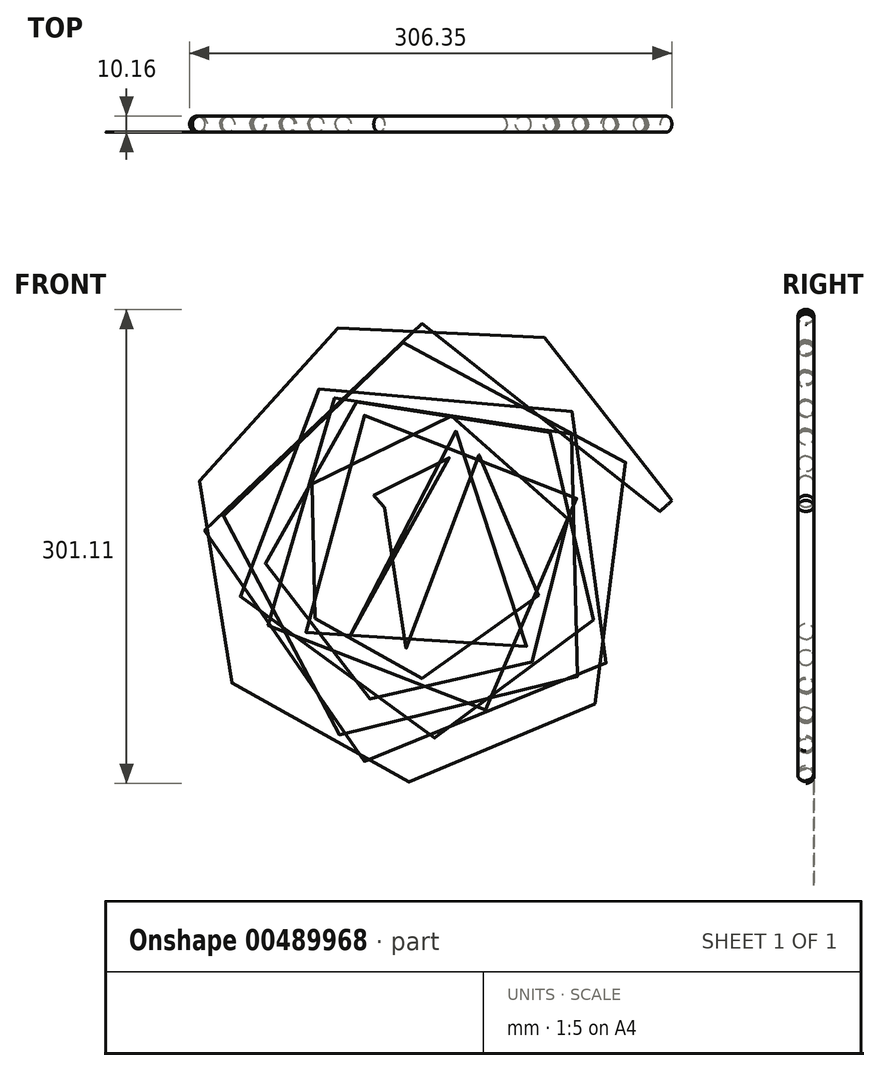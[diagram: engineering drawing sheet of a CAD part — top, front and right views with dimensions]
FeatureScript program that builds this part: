
annotation { "Feature Type Name" : "Feature", "Feature Type Description" : "" }
export const myFeature = defineFeature(function(context is Context, id is Id, definition is map)
    precondition{}
    {
        {
            var Q0;
            Q0=qCreatedBy(makeId("Top.planeOp"),FACE);
            var sketch = newSketch(context, id + "F0", { "sketchPlane" : qUnion([Q0])});
            skCircle(sketch, "E0", {"center": v(0, 0) * mm, "radius": 125 * mm});
            skSolve(sketch);
        }
        {
            var Q0;
            Q0=makeQuery(id+"F0.imprint","IMPRINT",FACE,{"disambiguationData":[TD([[makeQuery(id+"F0.imprint","IMPRINT",EDGE,{"derivedFrom":sQuery(id+"F0.wireOp",EDGE,"E0")}),1.0]])]});
            extrude(context, id + "F1", {"entities" : qUnion([Q0]), "depth" : 25 * mm, "offsetDistance" : 25 * mm});
        }
        {
            var Q0;
            Q0=makeQuery(id+"F1.opExtrude","SWEPT_BODY",BODY,{"disambiguationData":[OSD([sQuery(id+"F0.wireOp",EDGE,"E0")])]});
            deleteBodies(context, id + "F2", {"entities" : qUnion([Q0])});
        }
        {
            var Q0;
            Q0=qCreatedBy(makeId("Front.planeOp"),FACE);
            var sketch = newSketch(context, id + "F3", { "sketchPlane" : qUnion([Q0])});
            skLineSegment(sketch, "E1", {"start": v(0, 0) * mm, "end": v(0, 148.72) * mm});
            skLineSegment(sketch, "E2", {"start": v(0, 148.72) * mm, "end": v(118.91, 0) * mm});
            skLineSegment(sketch, "E3", {"start": v(118.91, 0) * mm, "end": v(0, 0) * mm});
            skSolve(sketch);
        }
        {
            var Q0;
            Q0=makeQuery(id+"F3.imprint","IMPRINT",FACE,{"disambiguationData":[TD([[makeQuery(id+"F3.imprint","IMPRINT",EDGE,{"derivedFrom":sQuery(id+"F3.wireOp",EDGE,"E1")}),-1.0]])]});
            var Q1;
            Q1=sQuery(id+"F3.wireOp",EDGE,"E1");
            revolve(context, id + "F4", {"entities" : qUnion([Q0]), "axis" : qUnion([Q1]), "revolveType" : RevolveType.FULL});
        }
        {
            var Q0;
            Q0=qCreatedBy(makeId("Top.planeOp"),FACE);
            var sketch = newSketch(context, id + "F5", { "sketchPlane" : qUnion([Q0])});
            skFitSpline(sketch, "E4.0", {"points": [v(118.91, 0) * mm, v(118.84, 2.92) * mm, v(118.65, 5.83) * mm, v(118.07, 11.63) * mm, v(117.67, 14.52) * mm, v(116.66, 20.24) * mm, v(116.05, 23.09) * mm, v(114.63, 28.72) * mm, v(113.82, 31.5) * mm, v(111.99, 37) * mm, v(110.97, 39.7) * mm, v(108.75, 45.05) * mm, v(107.54, 47.67) * mm, v(104.93, 52.82) * mm, v(103.54, 55.34) * mm, v(100.56, 60.28) * mm, v(98.99, 62.69) * mm, v(95.67, 67.38) * mm, v(93.92, 69.66) * mm, v(90.27, 74.09) * mm, v(88.37, 76.23) * mm, v(84.4, 80.37) * mm, v(82.36, 82.36) * mm, v(78.11, 86.18) * mm, v(75.92, 88.02) * mm, v(71.42, 91.51) * mm, v(69.1, 93.18) * mm, v(64.36, 96.33) * mm, v(61.94, 97.81) * mm, v(56.99, 100.6) * mm, v(54.46, 101.9) * mm, v(49.33, 104.3) * mm, v(46.73, 105.42) * mm, v(41.44, 107.44) * mm, v(38.77, 108.35) * mm, v(33.36, 109.97) * mm, v(30.63, 110.68) * mm, v(25.13, 111.9) * mm, v(22.36, 112.4) * mm, v(16.8, 113.22) * mm, v(14, 113.52) * mm, v(8.4, 113.92) * mm, v(5.6, 114) * mm, v(0, 114) * mm, v(-2.8, 113.88) * mm, v(-8.37, 113.45) * mm, v(-11.15, 113.13) * mm, v(-16.66, 112.3) * mm, v(-19.4, 111.78) * mm, v(-24.82, 110.54) * mm, v(-27.51, 109.82) * mm, v(-32.82, 108.2) * mm, v(-35.44, 107.28) * mm, v(-40.6, 105.27) * mm, v(-43.15, 104.17) * mm, v(-48.14, 101.79) * mm, v(-50.6, 100.5) * mm, v(-55.39, 97.77) * mm, v(-57.73, 96.31) * mm, v(-62.3, 93.24) * mm, v(-64.52, 91.61) * mm, v(-68.85, 88.22) * mm, v(-70.94, 86.44) * mm, v(-75, 82.74) * mm, v(-76.95, 80.82) * mm, v(-80.7, 76.84) * mm, v(-82.51, 74.78) * mm, v(-85.96, 70.55) * mm, v(-87.6, 68.37) * mm, v(-90.73, 63.9) * mm, v(-92.2, 61.6) * mm, v(-94.99, 56.93) * mm, v(-96.29, 54.54) * mm, v(-98.7, 49.68) * mm, v(-99.83, 47.21) * mm, v(-101.88, 42.2) * mm, v(-102.81, 39.66) * mm, v(-104.49, 34.52) * mm, v(-105.23, 31.92) * mm, v(-106.52, 26.68) * mm, v(-107.07, 24.04) * mm, v(-107.97, 18.73) * mm, v(-108.32, 16.06) * mm, v(-108.82, 10.72) * mm, v(-108.97, 8.04) * mm, v(-109.08, 2.68) * mm, v(-109.04, 0) * mm, v(-108.75, -5.34) * mm, v(-108.5, -8) * mm, v(-107.83, -13.3) * mm, v(-107.4, -15.93) * mm, v(-106.33, -21.15) * mm, v(-105.7, -23.74) * mm, v(-104.27, -28.86) * mm, v(-103.45, -31.38) * mm, v(-101.64, -36.37) * mm, v(-100.65, -38.83) * mm, v(-98.48, -43.65) * mm, v(-97.3, -46.03) * mm, v(-94.8, -50.67) * mm, v(-93.45, -52.94) * mm, v(-90.61, -57.38) * mm, v(-89.11, -59.55) * mm, v(-85.96, -63.75) * mm, v(-84.3, -65.8) * mm, v(-80.86, -69.75) * mm, v(-79.07, -71.67) * mm, v(-75.35, -75.35) * mm, v(-73.42, -77.12) * mm, v(-69.45, -80.51) * mm, v(-67.4, -82.13) * mm, v(-63.2, -85.22) * mm, v(-61.04, -86.68) * mm, v(-56.63, -89.44) * mm, v(-54.38, -90.73) * mm, v(-49.8, -93.16) * mm, v(-47.45, -94.28) * mm, v(-42.7, -96.35) * mm, v(-40.3, -97.3) * mm, v(-35.43, -99.02) * mm, v(-32.96, -99.78) * mm, v(-27.99, -101.13) * mm, v(-25.48, -101.71) * mm, v(-20.42, -102.69) * mm, v(-17.88, -103.08) * mm, v(-12.79, -103.68) * mm, v(-10.23, -103.89) * mm, v(-5.11, -104.1) * mm, v(-2.55, -104.13) * mm, v(2.55, -103.97) * mm, v(5.1, -103.8) * mm, v(10.17, -103.27) * mm, v(12.7, -102.91) * mm, v(17.7, -102.01) * mm, v(20.19, -101.47) * mm, v(25.1, -100.2) * mm, v(27.53, -99.49) * mm, v(32.33, -97.87) * mm, v(34.7, -96.97) * mm, v(39.36, -95.01) * mm, v(41.65, -93.95) * mm, v(46.14, -91.65) * mm, v(48.33, -90.42) * mm, v(52.63, -87.81) * mm, v(54.73, -86.43) * mm, v(58.82, -83.51) * mm, v(60.8, -81.98) * mm, v(64.65, -78.78) * mm, v(66.52, -77.1) * mm, v(70.11, -73.64) * mm, v(71.84, -71.84) * mm, v(75.17, -68.13) * mm, v(76.76, -66.2) * mm, v(79.8, -62.27) * mm, v(81.24, -60.25) * mm, v(83.96, -56.1) * mm, v(85.25, -53.98) * mm, v(87.66, -49.66) * mm, v(88.79, -47.45) * mm, v(90.87, -42.98) * mm, v(91.82, -40.7) * mm, v(93.57, -36.1) * mm, v(94.35, -33.76) * mm, v(95.75, -29.04) * mm, v(96.35, -26.66) * mm, v(97.4, -21.87) * mm, v(97.83, -19.46) * mm, v(98.51, -14.61) * mm, v(98.76, -12.18) * mm, v(99.09, -7.3) * mm, v(99.16, -4.87) * mm, v(99.12, 0) * mm, v(99.02, 2.43) * mm, v(98.62, 7.28) * mm, v(98.34, 9.69) * mm, v(97.6, 14.48) * mm, v(97.13, 16.86) * mm, v(96.03, 21.57) * mm, v(95.4, 23.9) * mm, v(93.97, 28.5) * mm, v(93.16, 30.78) * mm, v(91.4, 35.26) * mm, v(90.43, 37.46) * mm, v(88.35, 41.79) * mm, v(87.22, 43.9) * mm, v(84.83, 48.06) * mm, v(83.56, 50.09) * mm, v(80.87, 54.04) * mm, v(79.46, 55.96) * mm, v(76.5, 59.7) * mm, v(74.95, 61.5) * mm, v(71.72, 65) * mm, v(70.05, 66.7) * mm, v(66.59, 69.94) * mm, v(64.8, 71.5) * mm, v(61.11, 74.47) * mm, v(59.22, 75.89) * mm, v(55.34, 78.57) * mm, v(53.35, 79.84) * mm, v(49.29, 82.23) * mm, v(47.21, 83.35) * mm, v(43, 85.43) * mm, v(40.86, 86.39) * mm, v(36.5, 88.14) * mm, v(34.3, 88.94) * mm, v(29.85, 90.37) * mm, v(27.6, 91) * mm, v(23.07, 92.1) * mm, v(20.78, 92.56) * mm, v(16.2, 93.32) * mm, v(13.88, 93.6) * mm, v(9.26, 94.02) * mm, v(6.94, 94.14) * mm, v(2.31, 94.22) * mm, v(0, 94.17) * mm, v(-4.61, 93.9) * mm, v(-6.91, 93.68) * mm, v(-11.48, 93.07) * mm, v(-13.75, 92.69) * mm, v(-18.25, 91.75) * mm, v(-20.48, 91.2) * mm, v(-24.89, 89.94) * mm, v(-27.07, 89.22) * mm, v(-31.36, 87.64) * mm, v(-33.47, 86.77) * mm, v(-37.63, 84.88) * mm, v(-39.67, 83.87) * mm, v(-43.66, 81.68) * mm, v(-45.62, 80.52) * mm, v(-49.43, 78.05) * mm, v(-51.29, 76.75) * mm, v(-54.9, 74.02) * mm, v(-56.65, 72.59) * mm, v(-60.04, 69.6) * mm, v(-61.68, 68.05) * mm, v(-64.84, 64.83) * mm, v(-66.35, 63.17) * mm, v(-69.25, 59.74) * mm, v(-70.64, 57.97) * mm, v(-73.27, 54.34) * mm, v(-74.52, 52.48) * mm, v(-76.88, 48.68) * mm, v(-77.98, 46.74) * mm, v(-80.04, 42.78) * mm, v(-81, 40.77) * mm, v(-82.76, 36.68) * mm, v(-83.57, 34.61) * mm, v(-85.02, 30.42) * mm, v(-85.67, 28.3) * mm, v(-86.8, 24.02) * mm, v(-87.29, 21.86) * mm, v(-88.1, 17.52) * mm, v(-88.43, 15.34) * mm, v(-88.92, 10.97) * mm, v(-89.1, 8.77) * mm, v(-89.26, 4.38) * mm, v(-89.26, 2.19) * mm, v(-89.1, -2.19) * mm, v(-88.95, -4.37) * mm, v(-88.47, -8.72) * mm, v(-88.16, -10.88) * mm, v(-87.36, -15.16) * mm, v(-86.89, -17.29) * mm, v(-85.79, -21.49) * mm, v(-85.16, -23.57) * mm, v(-83.75, -27.67) * mm, v(-82.97, -29.7) * mm, v(-81.28, -33.67) * mm, v(-80.35, -35.62) * mm, v(-78.37, -39.45) * mm, v(-77.31, -41.33) * mm, v(-75.06, -44.99) * mm, v(-73.86, -46.78) * mm, v(-71.35, -50.26) * mm, v(-70.04, -51.95) * mm, v(-67.28, -55.22) * mm, v(-65.85, -56.8) * mm, v(-62.87, -59.86) * mm, v(-61.33, -61.33) * mm, v(-58.14, -64.15) * mm, v(-56.5, -65.5) * mm, v(-53.12, -68.07) * mm, v(-51.39, -69.3) * mm, v(-47.84, -71.6) * mm, v(-46.03, -72.69) * mm, v(-42.33, -74.73) * mm, v(-40.45, -75.67) * mm, v(-36.62, -77.43) * mm, v(-34.68, -78.23) * mm, v(-30.74, -79.7) * mm, v(-28.75, -80.35) * mm, v(-24.73, -81.52) * mm, v(-22.7, -82.02) * mm, v(-18.61, -82.89) * mm, v(-16.56, -83.24) * mm, v(-12.43, -83.8) * mm, v(-10.36, -84) * mm, v(-6.21, -84.26) * mm, v(-4.14, -84.3) * mm, v(0, -84.26) * mm, v(2.07, -84.15) * mm, v(6.18, -83.8) * mm, v(8.23, -83.54) * mm, v(12.3, -82.88) * mm, v(14.31, -82.48) * mm, v(18.3, -81.53) * mm, v(20.29, -80.98) * mm, v(24.19, -79.74) * mm, v(26.12, -79.05) * mm, v(29.9, -77.53) * mm, v(31.77, -76.7) * mm, v(35.43, -74.9) * mm, v(37.22, -73.94) * mm, v(40.73, -71.9) * mm, v(42.44, -70.8) * mm, v(45.78, -68.5) * mm, v(47.4, -67.3) * mm, v(50.55, -64.77) * mm, v(52.08, -63.45) * mm, v(55.02, -60.7) * mm, v(56.44, -59.28) * mm, v(59.17, -56.33) * mm, v(60.48, -54.81) * mm, v(62.98, -51.68) * mm, v(64.16, -50.07) * mm, v(66.42, -46.77) * mm, v(67.48, -45.09) * mm, v(69.48, -41.64) * mm, v(70.41, -39.89) * mm, v(72.15, -36.31) * mm, v(72.95, -34.5) * mm, v(74.4, -30.82) * mm, v(75.07, -28.96) * mm, v(76.25, -25.19) * mm, v(76.77, -23.29) * mm, v(77.67, -19.45) * mm, v(78.05, -17.52) * mm, v(78.67, -13.65) * mm, v(78.9, -11.7) * mm, v(79.23, -7.8) * mm, v(79.32, -5.85) * mm, v(79.35, -1.95) * mm, v(79.3, 0) * mm, v(79.05, 3.88) * mm, v(78.85, 5.82) * mm, v(78.32, 9.66) * mm, v(77.98, 11.57) * mm, v(77.17, 15.35) * mm, v(76.7, 17.22) * mm, v(75.6, 20.92) * mm, v(75, 22.75) * mm, v(73.64, 26.35) * mm, v(72.9, 28.12) * mm, v(71.3, 31.6) * mm, v(70.42, 33.31) * mm, v(68.57, 36.65) * mm, v(67.58, 38.29) * mm, v(65.5, 41.47) * mm, v(64.39, 43.03) * mm, v(62.08, 46.04) * mm, v(60.87, 47.5) * mm, v(58.34, 50.33) * mm, v(57.03, 51.7) * mm, v(54.32, 54.32) * mm, v(52.92, 55.58) * mm, v(50.02, 58) * mm, v(48.54, 59.15) * mm, v(45.48, 61.33) * mm, v(43.92, 62.37) * mm, v(40.72, 64.31) * mm, v(39.1, 65.23) * mm, v(35.77, 66.93) * mm, v(34.08, 67.72) * mm, v(30.66, 69.17) * mm, v(28.92, 69.83) * mm, v(25.4, 71.02) * mm, v(23.63, 71.55) * mm, v(20.05, 72.47) * mm, v(18.25, 72.87) * mm, v(14.62, 73.52) * mm, v(12.8, 73.78) * mm, v(9.15, 74.17) * mm, v(7.31, 74.3) * mm, v(3.65, 74.4) * mm, v(1.82, 74.4) * mm, v(-1.82, 74.24) * mm, v(-3.64, 74.1) * mm, v(-7.26, 73.68) * mm, v(-9.06, 73.4) * mm, v(-12.62, 72.71) * mm, v(-14.38, 72.3) * mm, v(-17.88, 71.36) * mm, v(-19.6, 70.83) * mm, v(-23, 69.63) * mm, v(-24.68, 68.98) * mm, v(-27.98, 67.54) * mm, v(-29.6, 66.76) * mm, v(-32.77, 65.09) * mm, v(-34.32, 64.2) * mm, v(-37.35, 62.3) * mm, v(-38.82, 61.3) * mm, v(-41.7, 59.2) * mm, v(-43.09, 58.1) * mm, v(-45.79, 55.8) * mm, v(-47.1, 54.6) * mm, v(-49.6, 52.1) * mm, v(-50.82, 50.81) * mm, v(-53.13, 48.16) * mm, v(-54.24, 46.79) * mm, v(-56.35, 43.97) * mm, v(-57.35, 42.53) * mm, v(-59.24, 39.58) * mm, v(-60.13, 38.07) * mm, v(-61.79, 35) * mm, v(-62.56, 33.44) * mm, v(-63.99, 30.26) * mm, v(-64.64, 28.65) * mm, v(-65.82, 25.39) * mm, v(-66.35, 23.74) * mm, v(-67.29, 20.41) * mm, v(-67.7, 18.73) * mm, v(-68.38, 15.35) * mm, v(-68.66, 13.66) * mm, v(-69.1, 10.25) * mm, v(-69.25, 8.54) * mm, v(-69.43, 5.12) * mm, v(-69.46, 3.4) * mm, v(-69.39, 0) * mm, v(-69.29, -1.7) * mm, v(-68.97, -5.09) * mm, v(-68.74, -6.77) * mm, v(-68.18, -10.11) * mm, v(-67.83, -11.77) * mm, v(-67.02, -15.05) * mm, v(-66.56, -16.67) * mm, v(-65.5, -19.87) * mm, v(-64.93, -21.45) * mm, v(-63.65, -24.56) * mm, v(-62.96, -26.08) * mm, v(-61.46, -29.07) * mm, v(-60.66, -30.54) * mm, v(-58.96, -33.4) * mm, v(-58.05, -34.8) * mm, v(-56.15, -37.52) * mm, v(-55.15, -38.84) * mm, v(-53.05, -41.4) * mm, v(-51.96, -42.64) * mm, v(-49.69, -45.04) * mm, v(-48.51, -46.2) * mm, v(-46.08, -48.4) * mm, v(-44.83, -49.46) * mm, v(-42.25, -51.48) * mm, v(-40.92, -52.44) * mm, v(-38.21, -54.26) * mm, v(-36.83, -55.12) * mm, v(-34, -56.73) * mm, v(-32.56, -57.48) * mm, v(-29.63, -58.87) * mm, v(-28.14, -59.5) * mm, v(-25.13, -60.67) * mm, v(-23.6, -61.2) * mm, v(-20.52, -62.13) * mm, v(-18.97, -62.55) * mm, v(-15.84, -63.25) * mm, v(-14.27, -63.55) * mm, v(-11.1, -64.02) * mm, v(-9.52, -64.2) * mm, v(-6.34, -64.43) * mm, v(-4.75, -64.49) * mm, v(-1.58, -64.49) * mm, v(0, -64.43) * mm, v(3.16, -64.2) * mm, v(4.72, -64.02) * mm, v(7.84, -63.56) * mm, v(9.39, -63.27) * mm, v(12.45, -62.58) * mm, v(13.97, -62.18) * mm, v(16.96, -61.28) * mm, v(18.44, -60.77) * mm, v(21.34, -59.64) * mm, v(22.77, -59.03) * mm, v(25.58, -57.7) * mm, v(26.95, -56.98) * mm, v(29.64, -55.46) * mm, v(30.96, -54.64) * mm, v(33.52, -52.93) * mm, v(34.76, -52.03) * mm, v(37.18, -50.13) * mm, v(38.35, -49.14) * mm, v(40.62, -47.09) * mm, v(41.71, -46.02) * mm, v(43.8, -43.8) * mm, v(44.81, -42.66) * mm, v(46.74, -40.31) * mm, v(47.65, -39.1) * mm, v(49.39, -36.63) * mm, v(50.2, -35.36) * mm, v(51.75, -32.77) * mm, v(52.48, -31.45) * mm, v(53.82, -28.76) * mm, v(54.44, -27.4) * mm, v(55.58, -24.63) * mm, v(56.1, -23.23) * mm, v(57.02, -20.4) * mm, v(57.43, -18.97) * mm, v(58.14, -16.09) * mm, v(58.44, -14.64) * mm, v(58.94, -11.72) * mm, v(59.13, -10.26) * mm, v(59.41, -7.33) * mm, v(59.5, -5.86) * mm, v(59.56, -2.92) * mm, v(59.53, -1.46) * mm, v(59.38, 1.46) * mm, v(59.25, 2.91) * mm, v(58.88, 5.8) * mm, v(58.64, 7.24) * mm, v(58.06, 10.08) * mm, v(57.72, 11.48) * mm, v(56.94, 14.26) * mm, v(56.5, 15.64) * mm, v(55.52, 18.34) * mm, v(54.98, 19.67) * mm, v(53.8, 22.29) * mm, v(53.17, 23.57) * mm, v(51.8, 26.08) * mm, v(51.08, 27.3) * mm, v(49.55, 29.7) * mm, v(48.74, 30.87) * mm, v(47.04, 33.13) * mm, v(46.15, 34.23) * mm, v(44.3, 36.36) * mm, v(43.33, 37.38) * mm, v(41.33, 39.36) * mm, v(40.3, 40.3) * mm, v(38.17, 42.12) * mm, v(37.07, 42.98) * mm, v(34.83, 44.63) * mm, v(33.67, 45.4) * mm, v(31.32, 46.88) * mm, v(30.12, 47.57) * mm, v(27.67, 48.85) * mm, v(26.43, 49.45) * mm, v(23.9, 50.54) * mm, v(22.62, 51.05) * mm, v(20.04, 51.95) * mm, v(18.73, 52.35) * mm, v(16.1, 53.06) * mm, v(14.77, 53.36) * mm, v(12.1, 53.87) * mm, v(10.75, 54.08) * mm, v(8.07, 54.39) * mm, v(6.72, 54.5) * mm, v(4.03, 54.6) * mm, v(2.68, 54.6) * mm, v(0, 54.52) * mm, v(-1.34, 54.42) * mm, v(-4, 54.14) * mm, v(-5.32, 53.95) * mm, v(-7.93, 53.47) * mm, v(-9.23, 53.18) * mm, v(-11.8, 52.51) * mm, v(-13.06, 52.13) * mm, v(-15.56, 51.28) * mm, v(-16.79, 50.8) * mm, v(-19.2, 49.78) * mm, v(-20.4, 49.22) * mm, v(-22.71, 48.02) * mm, v(-23.85, 47.38) * mm, v(-26.07, 46.02) * mm, v(-27.15, 45.3) * mm, v(-29.26, 43.78) * mm, v(-30.28, 42.99) * mm, v(-32.26, 41.33) * mm, v(-33.21, 40.47) * mm, v(-35.05, 38.67) * mm, v(-35.94, 37.74) * mm, v(-37.63, 35.83) * mm, v(-38.45, 34.84) * mm, v(-39.99, 32.82) * mm, v(-40.72, 31.78) * mm, v(-42.1, 29.65) * mm, v(-42.76, 28.57) * mm, v(-43.97, 26.35) * mm, v(-44.54, 25.23) * mm, v(-45.58, 22.94) * mm, v(-46.06, 21.78) * mm, v(-46.93, 19.44) * mm, v(-47.33, 18.25) * mm, v(-48.02, 15.86) * mm, v(-48.32, 14.65) * mm, v(-48.83, 12.23) * mm, v(-49.04, 11) * mm, v(-49.37, 8.56) * mm, v(-49.49, 7.34) * mm, v(-49.63, 4.89) * mm, v(-49.66, 3.66) * mm, v(-49.62, 1.22) * mm, v(-49.56, 0) * mm, v(-49.35, -2.43) * mm, v(-49.2, -3.63) * mm, v(-48.8, -6.02) * mm, v(-48.57, -7.2) * mm, v(-48, -9.55) * mm, v(-47.68, -10.7) * mm, v(-46.95, -13) * mm, v(-46.54, -14.12) * mm, v(-45.64, -16.33) * mm, v(-45.16, -17.42) * mm, v(-44.1, -19.55) * mm, v(-43.54, -20.6) * mm, v(-42.34, -22.63) * mm, v(-41.7, -23.63) * mm, v(-40.37, -25.56) * mm, v(-39.66, -26.5) * mm, v(-38.2, -28.33) * mm, v(-37.42, -29.2) * mm, v(-35.83, -30.9) * mm, v(-35, -31.73) * mm, v(-33.3, -33.3) * mm, v(-32.41, -34.05) * mm, v(-30.6, -35.48) * mm, v(-29.67, -36.16) * mm, v(-27.77, -37.45) * mm, v(-26.8, -38.05) * mm, v(-24.82, -39.2) * mm, v(-23.8, -39.72) * mm, v(-21.76, -40.7) * mm, v(-20.71, -41.16) * mm, v(-18.6, -41.98) * mm, v(-17.54, -42.36) * mm, v(-15.4, -43.02) * mm, v(-14.3, -43.31) * mm, v(-12.12, -43.81) * mm, v(-11.02, -44.02) * mm, v(-8.82, -44.36) * mm, v(-7.72, -44.48) * mm, v(-5.5, -44.65) * mm, v(-4.4, -44.7) * mm, v(-2.2, -44.7) * mm, v(-1.1, -44.67) * mm, v(1.1, -44.51) * mm, v(2.18, -44.4) * mm, v(4.34, -44.08) * mm, v(5.41, -43.89) * mm, v(7.53, -43.41) * mm, v(8.58, -43.14) * mm, v(10.65, -42.52) * mm, v(11.67, -42.17) * mm, v(13.68, -41.4) * mm, v(14.66, -40.98) * mm, v(16.6, -40.06) * mm, v(18.5, -39.08) * mm, v(20.3, -37.97) * mm, v(22.06, -36.8) * mm, v(22.91, -36.18) * mm, v(24.57, -34.89) * mm, v(25.37, -34.2) * mm, v(26.92, -32.8) * mm, v(27.67, -32.07) * mm, v(29.1, -30.57) * mm, v(29.8, -29.79) * mm, v(31.1, -28.19) * mm, v(31.72, -27.36) * mm, v(32.9, -25.68) * mm, v(33.47, -24.82) * mm, v(34.51, -23.06) * mm, v(35, -22.16) * mm, v(35.91, -20.34) * mm, v(36.33, -19.42) * mm, v(37.1, -17.55) * mm, v(37.45, -16.6) * mm, v(38.08, -14.69) * mm, v(38.35, -13.72) * mm, v(38.83, -11.78) * mm, v(39.03, -10.8) * mm, v(39.37, -8.84) * mm, v(39.5, -7.85) * mm, v(39.68, -5.88) * mm, v(39.74, -4.9) * mm, v(39.77, -2.93) * mm, v(39.76, -1.95) * mm, v(39.65, 0) * mm, v(39.56, 0.97) * mm, v(39.31, 2.9) * mm, v(39.15, 3.86) * mm, v(38.76, 5.75) * mm, v(38.53, 6.69) * mm, v(38, 8.54) * mm, v(37.41, 10.36) * mm, v(36.33, 13) * mm, v(35.06, 15.55) * mm, v(33.62, 17.98) * mm, v(32, 20.28) * mm, v(30.83, 21.72) * mm, v(29.6, 23.1) * mm, v(28.97, 23.78) * mm, v(27.66, 25.07) * mm, v(26.98, 25.69) * mm, v(25.58, 26.87) * mm, v(24.86, 27.43) * mm, v(23.38, 28.5) * mm, v(22.63, 29) * mm, v(21.1, 29.95) * mm, v(20.3, 30.4) * mm, v(18.71, 31.22) * mm, v(17.9, 31.6) * mm, v(16.26, 32.3) * mm, v(15.43, 32.62) * mm, v(13.75, 33.2) * mm, v(12.9, 33.45) * mm, v(11.2, 33.9) * mm, v(10.34, 34.09) * mm, v(8.62, 34.4) * mm, v(7.75, 34.53) * mm, v(6.02, 34.72) * mm, v(5.16, 34.78) * mm, v(3.43, 34.83) * mm, v(2.57, 34.83) * mm, v(0.85, 34.76) * mm, v(-0.86, 34.63) * mm, v(-3.38, 34.24) * mm, v(-5.85, 33.67) * mm, v(-8.25, 32.92) * mm, v(-10.58, 32) * mm, v(-12.82, 30.92) * mm, v(-14.95, 29.69) * mm, v(-16.98, 28.31) * mm, v(-18.88, 26.8) * mm, v(-20.65, 25.15) * mm, v(-22.28, 23.4) * mm, v(-23.77, 21.54) * mm, v(-24.66, 20.24) * mm, v(-25.5, 18.91) * mm, v(-25.9, 18.24) * mm, v(-26.63, 16.86) * mm, v(-26.97, 16.16) * mm, v(-27.6, 14.75) * mm, v(-27.88, 14.03) * mm, v(-28.4, 12.58) * mm, v(-28.85, 11.12) * mm, v(-29.37, 8.9) * mm, v(-29.71, 6.67) * mm, v(-29.9, 4.43) * mm, v(-29.9, 2.2) * mm, v(-29.76, 0) * mm, v(-29.44, -2.18) * mm, v(-28.97, -4.3) * mm, v(-28.35, -6.37) * mm, v(-27.58, -8.37) * mm, v(-26.67, -10.3) * mm, v(-25.63, -12.13) * mm, v(-24.47, -13.87) * mm, v(-23.2, -15.5) * mm, v(-21.8, -17.02) * mm, v(-20.32, -18.43) * mm, v(-18.75, -19.7) * mm, v(-17.1, -20.85) * mm, v(-15.39, -21.86) * mm, v(-13.62, -22.73) * mm, v(-11.8, -23.47) * mm, v(-9.96, -24.06) * mm, v(-8.09, -24.5) * mm, v(-6.2, -24.8) * mm, v(-4.33, -24.97) * mm, v(-2.46, -24.99) * mm, v(-0.6, -24.87) * mm, v(1.21, -24.61) * mm, v(3, -24.22) * mm, v(4.72, -23.71) * mm, v(6.4, -23.07) * mm, v(8, -22.32) * mm, v(9.52, -21.46) * mm, v(10.96, -20.5) * mm, v(12.32, -19.44) * mm, v(13.58, -18.3) * mm, v(14.73, -17.07) * mm, v(15.78, -15.78) * mm, v(16.73, -14.42) * mm, v(17.55, -13.01) * mm, v(18.27, -11.56) * mm, v(18.86, -10.08) * mm, v(19.34, -8.57) * mm, v(19.7, -7.04) * mm, v(19.94, -5.51) * mm, v(20.06, -3.99) * mm, v(20.07, -2.47) * mm, v(19.97, -0.98) * mm, v(19.75, 0.5) * mm, v(19.43, 1.92) * mm, v(19, 3.3) * mm, v(18.49, 4.64) * mm, v(17.88, 5.91) * mm, v(17.18, 7.12) * mm, v(16.4, 8.26) * mm, v(15.55, 9.33) * mm, v(14.63, 10.31) * mm, v(13.65, 11.21) * mm, v(12.62, 12.03) * mm, v(11.55, 12.75) * mm, v(10.44, 13.38) * mm, v(9.3, 13.92) * mm, v(8.13, 14.36) * mm, v(6.95, 14.71) * mm, v(5.77, 14.97) * mm, v(4.58, 15.13) * mm, v(3.4, 15.2) * mm, v(2.25, 15.18) * mm, v(1.1, 15.07) * mm, v(0, 14.88) * mm, v(-1.08, 14.6) * mm, v(-2.12, 14.26) * mm, v(-3.11, 13.83) * mm, v(-4.05, 13.35) * mm, v(-4.94, 12.8) * mm, v(-5.77, 12.19) * mm, v(-6.54, 11.53) * mm, v(-7.24, 10.82) * mm, v(-7.87, 10.08) * mm, v(-8.43, 9.3) * mm, v(-8.93, 8.5) * mm, v(-9.35, 7.66) * mm, v(-9.7, 6.82) * mm, v(-9.97, 5.97) * mm, v(-10.18, 5.12) * mm, v(-10.31, 4.26) * mm, v(-10.38, 3.42) * mm, v(-10.37, 2.6) * mm, v(-10.3, 1.78) * mm, v(-10.18, 1) * mm, v(-10, 0.24) * mm, v(-9.75, -0.48) * mm, v(-9.46, -1.17) * mm, v(-9.12, -1.82) * mm, v(-8.74, -2.42) * mm, v(-8.32, -2.98) * mm, v(-7.86, -3.5) * mm, v(-7.38, -3.95) * mm, v(-6.87, -4.36) * mm, v(-6.34, -4.71) * mm, v(-5.8, -5.01) * mm, v(-5.26, -5.26) * mm, v(-4.7, -5.46) * mm, v(-4.15, -5.6) * mm, v(-3.6, -5.7) * mm, v(-3.06, -5.74) * mm, v(-2.54, -5.74) * mm, v(-2.03, -5.7) * mm, v(-1.54, -5.6) * mm, v(-1.08, -5.47) * mm, v(-0.65, -5.3) * mm, v(-0.25, -5.1) * mm, v(0.13, -4.88) * mm, v(0.46, -4.63) * mm, v(0.76, -4.35) * mm, v(1.02, -4.06) * mm, v(1.25, -3.75) * mm, v(1.43, -3.43) * mm, v(1.57, -3.11) * mm, v(1.68, -2.79) * mm, v(1.74, -2.47) * mm, v(1.77, -2.15) * mm, v(1.77, -1.85) * mm, v(1.73, -1.56) * mm, v(1.65, -1.28) * mm, v(1.55, -1.03) * mm, v(1.42, -0.8) * mm, v(1.26, -0.6) * mm, v(1.09, -0.41) * mm, v(0.9, -0.26) * mm, v(0.68, -0.15) * mm, v(0.46, -0.06) * mm, v(0.23, -0.01) * mm, v(0.08, 0) * mm, v(0, 0) * mm]});
            skSolve(sketch);
        }
        {
            var Q0;
            Q0=sQuery(id+"F5.wireOp",VERTEX,"E4.0.start");
            var Q1;
            Q1=sQuery(id+"F5.wireOp",EDGE,"E4.0");
            cPlane(context, id + "F6", {"entities" : qUnion([Q0, Q1]), "cplaneType" : CPlaneType.CURVE_POINT, "offset" : 25 * mm, "width" : 150 * mm, "height" : 150 * mm});
        }
        {
            var Q0;
            Q0=qCreatedBy(makeId("Front.planeOp"),FACE);
            var sketch = newSketch(context, id + "F7", { "sketchPlane" : qUnion([Q0])});
            skFitSpline(sketch, "E5.0", {"points": [v(55.4, 69.58) * mm, v(55.33, 72.5) * mm, v(55.14, 75.42) * mm, v(54.56, 81.21) * mm, v(54.16, 84.1) * mm, v(53.15, 89.83) * mm, v(52.54, 92.67) * mm, v(51.12, 98.3) * mm, v(50.3, 101.08) * mm, v(48.48, 106.58) * mm, v(47.46, 109.3) * mm, v(45.24, 114.63) * mm, v(44.03, 117.26) * mm, v(41.42, 122.4) * mm, v(40.03, 124.93) * mm, v(37.05, 129.86) * mm, v(35.48, 132.27) * mm, v(32.16, 136.96) * mm, v(30.41, 139.24) * mm, v(26.76, 143.67) * mm, v(24.86, 145.81) * mm, v(20.9, 149.95) * mm, v(18.85, 151.94) * mm, v(14.6, 155.77) * mm, v(12.41, 157.6) * mm, v(7.9, 161.1) * mm, v(5.6, 162.76) * mm, v(0.85, 165.91) * mm, v(-1.57, 167.4) * mm, v(-6.52, 170.18) * mm, v(-9.05, 171.48) * mm, v(-14.18, 173.9) * mm, v(-16.78, 175) * mm, v(-22.07, 177.02) * mm, v(-24.74, 177.93) * mm, v(-30.15, 179.56) * mm, v(-32.88, 180.27) * mm, v(-38.38, 181.49) * mm, v(-41.15, 182) * mm, v(-46.72, 182.8) * mm, v(-49.51, 183.1) * mm, v(-55.1, 183.5) * mm, v(-57.91, 183.6) * mm, v(-63.51, 183.58) * mm, v(-66.3, 183.46) * mm, v(-71.88, 183.04) * mm, v(-74.66, 182.72) * mm, v(-80.17, 181.88) * mm, v(-82.9, 181.36) * mm, v(-88.33, 180.13) * mm, v(-91.02, 179.4) * mm, v(-96.33, 177.78) * mm, v(-98.95, 176.87) * mm, v(-104.12, 174.85) * mm, v(-106.66, 173.75) * mm, v(-111.65, 171.37) * mm, v(-114.1, 170.09) * mm, v(-118.9, 167.35) * mm, v(-121.24, 165.9) * mm, v(-125.8, 162.82) * mm, v(-128.03, 161.2) * mm, v(-132.36, 157.8) * mm, v(-134.45, 156.02) * mm, v(-138.5, 152.32) * mm, v(-140.46, 150.4) * mm, v(-144.22, 146.42) * mm, v(-146.02, 144.37) * mm, v(-149.47, 140.13) * mm, v(-151.12, 137.95) * mm, v(-154.24, 133.48) * mm, v(-155.72, 131.2) * mm, v(-158.5, 126.51) * mm, v(-159.8, 124.13) * mm, v(-162.22, 119.27) * mm, v(-163.34, 116.8) * mm, v(-165.4, 111.78) * mm, v(-166.32, 109.24) * mm, v(-168, 104.1) * mm, v(-168.74, 101.5) * mm, v(-170.03, 96.26) * mm, v(-170.58, 93.62) * mm, v(-171.47, 88.32) * mm, v(-171.83, 85.65) * mm, v(-172.33, 80.3) * mm, v(-172.48, 77.62) * mm, v(-172.6, 72.26) * mm, v(-172.55, 69.58) * mm, v(-172.26, 64.24) * mm, v(-172.02, 61.58) * mm, v(-171.34, 56.28) * mm, v(-170.9, 53.65) * mm, v(-169.84, 48.43) * mm, v(-169.22, 45.84) * mm, v(-167.77, 40.73) * mm, v(-166.96, 38.2) * mm, v(-165.15, 33.21) * mm, v(-164.15, 30.76) * mm, v(-161.99, 25.93) * mm, v(-160.82, 23.56) * mm, v(-158.3, 18.91) * mm, v(-156.96, 16.64) * mm, v(-154.12, 12.2) * mm, v(-152.62, 10.04) * mm, v(-149.47, 5.83) * mm, v(-147.82, 3.79) * mm, v(-144.37, -0.17) * mm, v(-142.58, -2.08) * mm, v(-138.86, -5.77) * mm, v(-136.93, -7.54) * mm, v(-132.96, -10.93) * mm, v(-130.91, -12.55) * mm, v(-126.7, -15.63) * mm, v(-124.55, -17.1) * mm, v(-120.14, -19.85) * mm, v(-117.9, -21.15) * mm, v(-113.3, -23.57) * mm, v(-110.96, -24.7) * mm, v(-106.22, -26.77) * mm, v(-103.81, -27.72) * mm, v(-98.94, -29.43) * mm, v(-96.47, -30.2) * mm, v(-91.5, -31.55) * mm, v(-88.98, -32.13) * mm, v(-83.93, -33.1) * mm, v(-81.4, -33.5) * mm, v(-76.3, -34.1) * mm, v(-73.74, -34.3) * mm, v(-68.62, -34.53) * mm, v(-66.06, -34.54) * mm, v(-60.96, -34.39) * mm, v(-58.4, -34.22) * mm, v(-53.34, -33.69) * mm, v(-50.81, -33.33) * mm, v(-45.8, -32.43) * mm, v(-43.32, -31.89) * mm, v(-38.4, -30.63) * mm, v(-35.98, -29.9) * mm, v(-31.18, -28.29) * mm, v(-28.8, -27.4) * mm, v(-24.15, -25.43) * mm, v(-21.86, -24.36) * mm, v(-17.37, -22.07) * mm, v(-15.17, -20.84) * mm, v(-10.88, -18.23) * mm, v(-8.78, -16.84) * mm, v(-4.7, -13.93) * mm, v(-2.7, -12.4) * mm, v(1.14, -9.2) * mm, v(3, -7.52) * mm, v(6.6, -4.06) * mm, v(8.34, -2.26) * mm, v(11.66, 1.46) * mm, v(13.25, 3.37) * mm, v(16.28, 7.31) * mm, v(17.73, 9.34) * mm, v(20.45, 13.48) * mm, v(21.74, 15.6) * mm, v(24.15, 19.93) * mm, v(25.28, 22.13) * mm, v(27.36, 26.6) * mm, v(28.31, 28.88) * mm, v(30.06, 33.5) * mm, v(30.84, 35.83) * mm, v(32.24, 40.54) * mm, v(32.84, 42.92) * mm, v(33.89, 47.71) * mm, v(34.32, 50.13) * mm, v(35, 54.97) * mm, v(35.25, 57.4) * mm, v(35.58, 62.28) * mm, v(35.65, 64.71) * mm, v(35.61, 69.59) * mm, v(35.5, 72.02) * mm, v(35.11, 76.86) * mm, v(34.83, 79.27) * mm, v(34.08, 84.06) * mm, v(33.62, 86.44) * mm, v(32.53, 91.15) * mm, v(31.9, 93.48) * mm, v(30.46, 98.09) * mm, v(29.65, 100.36) * mm, v(27.89, 104.84) * mm, v(26.92, 107.04) * mm, v(24.84, 111.37) * mm, v(23.71, 113.5) * mm, v(21.32, 117.64) * mm, v(20.05, 119.67) * mm, v(17.36, 123.62) * mm, v(15.95, 125.55) * mm, v(12.98, 129.28) * mm, v(11.44, 131.1) * mm, v(8.21, 134.6) * mm, v(6.54, 136.28) * mm, v(3.08, 139.52) * mm, v(1.29, 141.08) * mm, v(-2.4, 144.05) * mm, v(-4.3, 145.47) * mm, v(-8.17, 148.16) * mm, v(-10.16, 149.43) * mm, v(-14.22, 151.82) * mm, v(-16.3, 152.93) * mm, v(-20.51, 155.01) * mm, v(-22.65, 155.97) * mm, v(-27, 157.73) * mm, v(-29.2, 158.53) * mm, v(-33.66, 159.95) * mm, v(-35.9, 160.59) * mm, v(-40.44, 161.68) * mm, v(-42.73, 162.14) * mm, v(-47.32, 162.9) * mm, v(-49.63, 163.2) * mm, v(-54.25, 163.6) * mm, v(-56.57, 163.73) * mm, v(-61.2, 163.8) * mm, v(-63.51, 163.75) * mm, v(-68.12, 163.48) * mm, v(-70.42, 163.26) * mm, v(-75, 162.66) * mm, v(-77.26, 162.27) * mm, v(-81.76, 161.33) * mm, v(-84, 160.78) * mm, v(-88.4, 159.52) * mm, v(-90.58, 158.8) * mm, v(-94.87, 157.23) * mm, v(-96.98, 156.36) * mm, v(-101.14, 154.47) * mm, v(-103.18, 153.45) * mm, v(-107.17, 151.27) * mm, v(-109.13, 150.1) * mm, v(-112.94, 147.64) * mm, v(-114.8, 146.33) * mm, v(-118.4, 143.6) * mm, v(-120.16, 142.17) * mm, v(-123.55, 139.19) * mm, v(-125.2, 137.63) * mm, v(-128.35, 134.42) * mm, v(-129.86, 132.75) * mm, v(-132.76, 129.32) * mm, v(-134.15, 127.55) * mm, v(-136.78, 123.93) * mm, v(-138.03, 122.07) * mm, v(-140.39, 118.26) * mm, v(-141.5, 116.32) * mm, v(-143.55, 112.37) * mm, v(-144.51, 110.35) * mm, v(-146.27, 106.27) * mm, v(-147.08, 104.2) * mm, v(-148.53, 100) * mm, v(-149.18, 97.88) * mm, v(-150.31, 93.6) * mm, v(-150.8, 91.45) * mm, v(-151.61, 87.1) * mm, v(-151.94, 84.93) * mm, v(-152.43, 80.55) * mm, v(-152.6, 78.36) * mm, v(-152.77, 73.97) * mm, v(-152.77, 71.77) * mm, v(-152.62, 67.4) * mm, v(-152.46, 65.21) * mm, v(-151.98, 60.87) * mm, v(-151.67, 58.7) * mm, v(-150.87, 54.42) * mm, v(-150.4, 52.3) * mm, v(-149.3, 48.1) * mm, v(-148.67, 46.01) * mm, v(-147.26, 41.91) * mm, v(-146.48, 39.9) * mm, v(-144.79, 35.92) * mm, v(-143.86, 33.96) * mm, v(-141.88, 30.13) * mm, v(-140.82, 28.26) * mm, v(-138.57, 24.6) * mm, v(-137.37, 22.8) * mm, v(-134.86, 19.33) * mm, v(-133.55, 17.64) * mm, v(-130.8, 14.36) * mm, v(-129.36, 12.78) * mm, v(-126.38, 9.72) * mm, v(-124.84, 8.25) * mm, v(-121.65, 5.43) * mm, v(-120, 4.08) * mm, v(-116.63, 1.51) * mm, v(-114.9, 0.3) * mm, v(-111.35, -2.02) * mm, v(-109.54, -3.1) * mm, v(-105.84, -5.14) * mm, v(-103.96, -6.09) * mm, v(-100.13, -7.84) * mm, v(-98.18, -8.65) * mm, v(-94.25, -10.11) * mm, v(-92.26, -10.77) * mm, v(-88.24, -11.93) * mm, v(-86.2, -12.44) * mm, v(-82.12, -13.3) * mm, v(-80.07, -13.66) * mm, v(-75.94, -14.22) * mm, v(-73.87, -14.42) * mm, v(-69.72, -14.68) * mm, v(-67.65, -14.72) * mm, v(-63.5, -14.67) * mm, v(-61.44, -14.57) * mm, v(-57.33, -14.21) * mm, v(-55.28, -13.96) * mm, v(-51.21, -13.3) * mm, v(-49.2, -12.9) * mm, v(-45.2, -11.94) * mm, v(-43.22, -11.4) * mm, v(-39.32, -10.15) * mm, v(-37.4, -9.46) * mm, v(-33.6, -7.94) * mm, v(-31.74, -7.11) * mm, v(-28.08, -5.32) * mm, v(-26.29, -4.36) * mm, v(-22.78, -2.3) * mm, v(-21.07, -1.22) * mm, v(-17.73, 1.07) * mm, v(-16.1, 2.28) * mm, v(-12.96, 4.81) * mm, v(-11.43, 6.13) * mm, v(-8.49, 8.88) * mm, v(-7.07, 10.3) * mm, v(-4.34, 13.25) * mm, v(-3.03, 14.77) * mm, v(-0.53, 17.9) * mm, v(0.66, 19.51) * mm, v(2.9, 22.8) * mm, v(3.97, 24.5) * mm, v(5.97, 27.94) * mm, v(6.9, 29.7) * mm, v(8.64, 33.27) * mm, v(9.44, 35.09) * mm, v(10.9, 38.76) * mm, v(11.56, 40.63) * mm, v(12.74, 44.4) * mm, v(13.26, 46.3) * mm, v(14.16, 50.13) * mm, v(14.54, 52.06) * mm, v(15.16, 55.94) * mm, v(15.4, 57.88) * mm, v(15.72, 61.78) * mm, v(15.8, 63.74) * mm, v(15.84, 67.64) * mm, v(15.79, 69.59) * mm, v(15.54, 73.47) * mm, v(15.34, 75.4) * mm, v(14.8, 79.24) * mm, v(14.47, 81.15) * mm, v(13.66, 84.93) * mm, v(13.18, 86.8) * mm, v(12.1, 90.5) * mm, v(11.48, 92.34) * mm, v(10.13, 95.93) * mm, v(9.4, 97.7) * mm, v(7.78, 101.19) * mm, v(6.91, 102.9) * mm, v(5.06, 106.24) * mm, v(4.07, 107.87) * mm, v(1.98, 111.06) * mm, v(0.88, 112.6) * mm, v(-1.43, 115.62) * mm, v(-2.64, 117.09) * mm, v(-5.17, 119.91) * mm, v(-6.48, 121.28) * mm, v(-9.2, 123.9) * mm, v(-10.6, 125.17) * mm, v(-13.49, 127.58) * mm, v(-14.97, 128.73) * mm, v(-18.03, 130.91) * mm, v(-19.59, 131.95) * mm, v(-22.78, 133.9) * mm, v(-24.42, 134.81) * mm, v(-27.74, 136.51) * mm, v(-29.42, 137.3) * mm, v(-32.85, 138.75) * mm, v(-34.59, 139.41) * mm, v(-38.1, 140.6) * mm, v(-39.88, 141.13) * mm, v(-43.46, 142.05) * mm, v(-45.26, 142.45) * mm, v(-48.89, 143.1) * mm, v(-50.7, 143.37) * mm, v(-54.36, 143.75) * mm, v(-56.2, 143.88) * mm, v(-59.86, 144) * mm, v(-61.69, 143.98) * mm, v(-65.33, 143.83) * mm, v(-67.15, 143.68) * mm, v(-70.77, 143.26) * mm, v(-72.56, 142.98) * mm, v(-76.13, 142.3) * mm, v(-77.9, 141.89) * mm, v(-81.39, 140.95) * mm, v(-83.11, 140.41) * mm, v(-86.52, 139.22) * mm, v(-88.2, 138.56) * mm, v(-91.49, 137.12) * mm, v(-93.1, 136.34) * mm, v(-96.27, 134.67) * mm, v(-97.83, 133.78) * mm, v(-100.86, 131.89) * mm, v(-102.33, 130.89) * mm, v(-105.2, 128.78) * mm, v(-106.6, 127.68) * mm, v(-109.3, 125.37) * mm, v(-110.6, 124.17) * mm, v(-113.12, 121.69) * mm, v(-114.33, 120.4) * mm, v(-116.64, 117.74) * mm, v(-117.75, 116.37) * mm, v(-119.86, 113.56) * mm, v(-120.86, 112.11) * mm, v(-122.75, 109.16) * mm, v(-123.64, 107.66) * mm, v(-125.3, 104.58) * mm, v(-126.07, 103.02) * mm, v(-127.5, 99.84) * mm, v(-128.15, 98.23) * mm, v(-129.33, 94.97) * mm, v(-129.86, 93.32) * mm, v(-130.8, 90) * mm, v(-131.2, 88.31) * mm, v(-131.9, 84.94) * mm, v(-132.17, 83.24) * mm, v(-132.6, 79.83) * mm, v(-132.76, 78.12) * mm, v(-132.94, 74.7) * mm, v(-132.97, 73) * mm, v(-132.9, 69.58) * mm, v(-132.8, 67.88) * mm, v(-132.48, 64.5) * mm, v(-132.25, 62.81) * mm, v(-131.69, 59.47) * mm, v(-131.34, 57.81) * mm, v(-130.53, 54.53) * mm, v(-130.07, 52.91) * mm, v(-129.02, 49.71) * mm, v(-128.44, 48.13) * mm, v(-127.16, 45.03) * mm, v(-126.47, 43.5) * mm, v(-124.97, 40.51) * mm, v(-124.17, 39.05) * mm, v(-122.47, 36.18) * mm, v(-121.56, 34.79) * mm, v(-119.66, 32.07) * mm, v(-118.66, 30.74) * mm, v(-116.56, 28.18) * mm, v(-115.47, 26.94) * mm, v(-113.2, 24.55) * mm, v(-112.02, 23.4) * mm, v(-109.6, 21.18) * mm, v(-108.34, 20.12) * mm, v(-105.76, 18.1) * mm, v(-104.43, 17.14) * mm, v(-101.72, 15.32) * mm, v(-100.34, 14.47) * mm, v(-97.5, 12.86) * mm, v(-96.07, 12.1) * mm, v(-93.14, 10.72) * mm, v(-91.65, 10.08) * mm, v(-88.64, 8.91) * mm, v(-87.11, 8.39) * mm, v(-84.03, 7.45) * mm, v(-82.48, 7.04) * mm, v(-79.35, 6.33) * mm, v(-77.78, 6.04) * mm, v(-74.62, 5.57) * mm, v(-73.03, 5.4) * mm, v(-69.85, 5.16) * mm, v(-68.26, 5.1) * mm, v(-65.1, 5.1) * mm, v(-63.5, 5.15) * mm, v(-60.35, 5.39) * mm, v(-58.78, 5.56) * mm, v(-55.67, 6.02) * mm, v(-54.12, 6.31) * mm, v(-51.06, 7) * mm, v(-49.54, 7.4) * mm, v(-46.55, 8.3) * mm, v(-45.07, 8.82) * mm, v(-42.17, 9.94) * mm, v(-40.74, 10.56) * mm, v(-37.93, 11.88) * mm, v(-36.56, 12.6) * mm, v(-33.87, 14.13) * mm, v(-32.55, 14.94) * mm, v(-30, 16.65) * mm, v(-28.74, 17.56) * mm, v(-26.33, 19.45) * mm, v(-25.15, 20.44) * mm, v(-22.9, 22.5) * mm, v(-21.8, 23.57) * mm, v(-19.7, 25.78) * mm, v(-18.7, 26.92) * mm, v(-16.77, 29.27) * mm, v(-15.86, 30.48) * mm, v(-14.12, 32.96) * mm, v(-13.3, 34.22) * mm, v(-11.76, 36.81) * mm, v(-11.03, 38.13) * mm, v(-9.7, 40.82) * mm, v(-9.07, 42.18) * mm, v(-7.93, 44.95) * mm, v(-7.42, 46.35) * mm, v(-6.5, 49.18) * mm, v(-6.08, 50.61) * mm, v(-5.37, 53.5) * mm, v(-5.07, 54.95) * mm, v(-4.57, 57.86) * mm, v(-4.38, 59.33) * mm, v(-4.1, 62.26) * mm, v(-4.01, 63.73) * mm, v(-3.95, 66.66) * mm, v(-3.98, 68.12) * mm, v(-4.13, 71.04) * mm, v(-4.26, 72.5) * mm, v(-4.63, 75.38) * mm, v(-4.87, 76.82) * mm, v(-5.45, 79.66) * mm, v(-5.79, 81.07) * mm, v(-6.57, 83.85) * mm, v(-7.01, 85.22) * mm, v(-8, 87.93) * mm, v(-8.53, 89.26) * mm, v(-9.7, 91.87) * mm, v(-10.34, 93.15) * mm, v(-11.7, 95.66) * mm, v(-12.43, 96.9) * mm, v(-13.96, 99.29) * mm, v(-14.77, 100.45) * mm, v(-16.47, 102.72) * mm, v(-17.36, 103.81) * mm, v(-19.21, 105.94) * mm, v(-20.18, 106.97) * mm, v(-22.18, 108.94) * mm, v(-23.2, 109.89) * mm, v(-25.34, 111.7) * mm, v(-26.43, 112.57) * mm, v(-28.68, 114.21) * mm, v(-29.84, 115) * mm, v(-32.19, 116.46) * mm, v(-33.4, 117.15) * mm, v(-35.84, 118.43) * mm, v(-37.08, 119.03) * mm, v(-39.6, 120.13) * mm, v(-40.89, 120.63) * mm, v(-43.47, 121.53) * mm, v(-44.78, 121.94) * mm, v(-47.42, 122.64) * mm, v(-48.74, 122.95) * mm, v(-51.41, 123.46) * mm, v(-52.76, 123.66) * mm, v(-55.44, 123.97) * mm, v(-56.8, 124.08) * mm, v(-59.48, 124.19) * mm, v(-60.83, 124.2) * mm, v(-63.51, 124.1) * mm, v(-64.85, 124) * mm, v(-67.5, 123.72) * mm, v(-68.83, 123.53) * mm, v(-71.44, 123.05) * mm, v(-72.74, 122.76) * mm, v(-75.3, 122.1) * mm, v(-76.57, 121.72) * mm, v(-79.07, 120.86) * mm, v(-80.3, 120.4) * mm, v(-82.71, 119.36) * mm, v(-83.9, 118.8) * mm, v(-86.22, 117.6) * mm, v(-87.36, 116.97) * mm, v(-89.58, 115.6) * mm, v(-90.66, 114.88) * mm, v(-92.77, 113.37) * mm, v(-93.79, 112.57) * mm, v(-95.77, 110.91) * mm, v(-96.72, 110.05) * mm, v(-98.56, 108.26) * mm, v(-99.45, 107.33) * mm, v(-101.14, 105.41) * mm, v(-101.96, 104.43) * mm, v(-103.5, 102.4) * mm, v(-104.23, 101.36) * mm, v(-105.61, 99.24) * mm, v(-106.27, 98.15) * mm, v(-107.48, 95.94) * mm, v(-108.05, 94.81) * mm, v(-109.1, 92.53) * mm, v(-109.57, 91.37) * mm, v(-110.44, 89.02) * mm, v(-110.84, 87.84) * mm, v(-111.53, 85.44) * mm, v(-111.83, 84.24) * mm, v(-112.34, 81.81) * mm, v(-112.55, 80.6) * mm, v(-112.88, 78.15) * mm, v(-113, 76.92) * mm, v(-113.14, 74.47) * mm, v(-113.17, 73.24) * mm, v(-113.13, 70.8) * mm, v(-113.07, 69.58) * mm, v(-112.86, 67.16) * mm, v(-112.7, 65.95) * mm, v(-112.31, 63.56) * mm, v(-112.08, 62.38) * mm, v(-111.51, 60.03) * mm, v(-111.19, 58.88) * mm, v(-110.45, 56.6) * mm, v(-110.05, 55.46) * mm, v(-109.15, 53.25) * mm, v(-108.67, 52.16) * mm, v(-107.62, 50.03) * mm, v(-107.05, 48.99) * mm, v(-105.85, 46.95) * mm, v(-105.22, 45.95) * mm, v(-103.88, 44.02) * mm, v(-103.17, 43.08) * mm, v(-101.7, 41.26) * mm, v(-100.93, 40.38) * mm, v(-99.34, 38.68) * mm, v(-98.5, 37.86) * mm, v(-96.8, 36.29) * mm, v(-95.92, 35.54) * mm, v(-94.11, 34.1) * mm, v(-93.18, 33.43) * mm, v(-91.28, 32.14) * mm, v(-90.3, 31.53) * mm, v(-88.33, 30.4) * mm, v(-87.32, 29.86) * mm, v(-85.27, 28.88) * mm, v(-84.22, 28.43) * mm, v(-82.12, 27.6) * mm, v(-81.05, 27.23) * mm, v(-78.9, 26.56) * mm, v(-77.82, 26.27) * mm, v(-75.63, 25.77) * mm, v(-74.53, 25.56) * mm, v(-72.33, 25.23) * mm, v(-71.23, 25.1) * mm, v(-69.02, 24.93) * mm, v(-67.91, 24.88) * mm, v(-65.7, 24.88) * mm, v(-64.6, 24.91) * mm, v(-62.42, 25.07) * mm, v(-61.33, 25.19) * mm, v(-59.17, 25.5) * mm, v(-58.1, 25.7) * mm, v(-55.97, 26.17) * mm, v(-54.93, 26.44) * mm, v(-52.86, 27.07) * mm, v(-51.84, 27.42) * mm, v(-49.83, 28.19) * mm, v(-48.85, 28.6) * mm, v(-46.91, 29.52) * mm, v(-45.02, 30.5) * mm, v(-43.21, 31.61) * mm, v(-41.45, 32.79) * mm, v(-40.6, 33.4) * mm, v(-38.94, 34.7) * mm, v(-38.14, 35.37) * mm, v(-36.59, 36.78) * mm, v(-35.84, 37.5) * mm, v(-34.4, 39.02) * mm, v(-33.72, 39.8) * mm, v(-32.4, 41.4) * mm, v(-31.78, 42.22) * mm, v(-30.6, 43.9) * mm, v(-30.04, 44.77) * mm, v(-29, 46.52) * mm, v(-28.5, 47.42) * mm, v(-27.6, 49.24) * mm, v(-27.18, 50.16) * mm, v(-26.4, 52.04) * mm, v(-26.06, 52.98) * mm, v(-25.43, 54.9) * mm, v(-25.16, 55.86) * mm, v(-24.68, 57.8) * mm, v(-24.48, 58.78) * mm, v(-24.14, 60.75) * mm, v(-24.01, 61.73) * mm, v(-23.83, 63.7) * mm, v(-23.77, 64.68) * mm, v(-23.74, 66.65) * mm, v(-23.75, 67.63) * mm, v(-23.86, 69.59) * mm, v(-23.95, 70.56) * mm, v(-24.2, 72.49) * mm, v(-24.36, 73.44) * mm, v(-24.75, 75.33) * mm, v(-24.98, 76.27) * mm, v(-25.5, 78.12) * mm, v(-26.1, 79.94) * mm, v(-27.18, 82.59) * mm, v(-28.45, 85.13) * mm, v(-29.9, 87.56) * mm, v(-31.5, 89.86) * mm, v(-32.68, 91.3) * mm, v(-33.9, 92.7) * mm, v(-34.54, 93.36) * mm, v(-35.85, 94.65) * mm, v(-36.53, 95.27) * mm, v(-37.93, 96.45) * mm, v(-38.65, 97.01) * mm, v(-40.13, 98.08) * mm, v(-40.88, 98.58) * mm, v(-42.42, 99.53) * mm, v(-43.2, 99.98) * mm, v(-44.8, 100.8) * mm, v(-45.6, 101.19) * mm, v(-47.25, 101.89) * mm, v(-48.08, 102.2) * mm, v(-49.76, 102.78) * mm, v(-50.6, 103.04) * mm, v(-52.31, 103.48) * mm, v(-53.17, 103.67) * mm, v(-54.9, 103.99) * mm, v(-55.76, 104.11) * mm, v(-57.49, 104.3) * mm, v(-58.35, 104.36) * mm, v(-60.08, 104.42) * mm, v(-60.94, 104.41) * mm, v(-62.66, 104.34) * mm, v(-64.37, 104.2) * mm, v(-66.89, 103.82) * mm, v(-69.36, 103.25) * mm, v(-71.76, 102.5) * mm, v(-74.09, 101.59) * mm, v(-76.33, 100.5) * mm, v(-78.46, 99.27) * mm, v(-80.48, 97.9) * mm, v(-82.39, 96.38) * mm, v(-84.16, 94.74) * mm, v(-85.8, 92.98) * mm, v(-87.28, 91.12) * mm, v(-88.17, 89.82) * mm, v(-89.01, 88.5) * mm, v(-89.4, 87.82) * mm, v(-90.14, 86.44) * mm, v(-90.48, 85.75) * mm, v(-91.1, 84.33) * mm, v(-91.39, 83.61) * mm, v(-91.9, 82.17) * mm, v(-92.36, 80.7) * mm, v(-92.88, 78.49) * mm, v(-93.22, 76.25) * mm, v(-93.4, 74.01) * mm, v(-93.42, 71.78) * mm, v(-93.26, 69.58) * mm, v(-92.95, 67.4) * mm, v(-92.48, 65.28) * mm, v(-91.86, 63.21) * mm, v(-91.1, 61.21) * mm, v(-90.18, 59.29) * mm, v(-89.14, 57.45) * mm, v(-87.98, 55.71) * mm, v(-86.7, 54.08) * mm, v(-85.31, 52.56) * mm, v(-83.83, 51.16) * mm, v(-82.26, 49.88) * mm, v(-80.61, 48.74) * mm, v(-78.9, 47.72) * mm, v(-77.13, 46.85) * mm, v(-75.32, 46.12) * mm, v(-73.47, 45.53) * mm, v(-71.6, 45.08) * mm, v(-69.72, 44.78) * mm, v(-67.84, 44.62) * mm, v(-65.96, 44.6) * mm, v(-64.11, 44.72) * mm, v(-62.3, 44.97) * mm, v(-60.52, 45.36) * mm, v(-58.79, 45.87) * mm, v(-57.12, 46.5) * mm, v(-55.52, 47.26) * mm, v(-54, 48.12) * mm, v(-52.55, 49.09) * mm, v(-51.2, 50.14) * mm, v(-49.93, 51.29) * mm, v(-48.78, 52.51) * mm, v(-47.73, 53.8) * mm, v(-46.78, 55.16) * mm, v(-45.96, 56.57) * mm, v(-45.24, 58.02) * mm, v(-44.65, 59.5) * mm, v(-44.17, 61.02) * mm, v(-43.8, 62.54) * mm, v(-43.57, 64.07) * mm, v(-43.45, 65.6) * mm, v(-43.44, 67.11) * mm, v(-43.54, 68.6) * mm, v(-43.76, 70.07) * mm, v(-44.08, 71.5) * mm, v(-44.5, 72.89) * mm, v(-45.02, 74.22) * mm, v(-45.63, 75.5) * mm, v(-46.33, 76.7) * mm, v(-47.1, 77.85) * mm, v(-47.96, 78.91) * mm, v(-48.88, 79.9) * mm, v(-49.86, 80.8) * mm, v(-50.89, 81.6) * mm, v(-51.96, 82.33) * mm, v(-53.07, 82.97) * mm, v(-54.22, 83.5) * mm, v(-55.38, 83.95) * mm, v(-56.56, 84.3) * mm, v(-57.74, 84.55) * mm, v(-58.93, 84.71) * mm, v(-60.1, 84.78) * mm, v(-61.26, 84.76) * mm, v(-62.4, 84.65) * mm, v(-63.52, 84.46) * mm, v(-64.6, 84.19) * mm, v(-65.63, 83.84) * mm, v(-66.62, 83.42) * mm, v(-67.56, 82.93) * mm, v(-68.45, 82.38) * mm, v(-69.28, 81.77) * mm, v(-70.05, 81.1) * mm, v(-70.75, 80.4) * mm, v(-71.38, 79.66) * mm, v(-71.94, 78.88) * mm, v(-72.44, 78.07) * mm, v(-72.86, 77.25) * mm, v(-73.2, 76.4) * mm, v(-73.48, 75.55) * mm, v(-73.69, 74.7) * mm, v(-73.82, 73.85) * mm, v(-73.89, 73) * mm, v(-73.88, 72.18) * mm, v(-73.82, 71.37) * mm, v(-73.69, 70.58) * mm, v(-73.5, 69.82) * mm, v(-73.26, 69.1) * mm, v(-72.97, 68.41) * mm, v(-72.63, 67.76) * mm, v(-72.25, 67.16) * mm, v(-71.82, 66.6) * mm, v(-71.37, 66.1) * mm, v(-70.89, 65.63) * mm, v(-70.38, 65.23) * mm, v(-69.85, 64.87) * mm, v(-69.31, 64.57) * mm, v(-68.77, 64.32) * mm, v(-68.21, 64.12) * mm, v(-67.66, 63.98) * mm, v(-67.11, 63.89) * mm, v(-66.57, 63.84) * mm, v(-66.05, 63.84) * mm, v(-65.54, 63.9) * mm, v(-65.05, 63.98) * mm, v(-64.6, 64.11) * mm, v(-64.16, 64.28) * mm, v(-63.76, 64.48) * mm, v(-63.38, 64.7) * mm, v(-63.05, 64.96) * mm, v(-62.75, 65.23) * mm, v(-62.49, 65.53) * mm, v(-62.26, 65.83) * mm, v(-62.08, 66.15) * mm, v(-61.94, 66.47) * mm, v(-61.83, 66.8) * mm, v(-61.77, 67.12) * mm, v(-61.74, 67.43) * mm, v(-61.74, 67.74) * mm, v(-61.78, 68.03) * mm, v(-61.86, 68.3) * mm, v(-61.96, 68.56) * mm, v(-62.1, 68.79) * mm, v(-62.25, 69) * mm, v(-62.42, 69.17) * mm, v(-62.62, 69.32) * mm, v(-62.83, 69.44) * mm, v(-63.05, 69.52) * mm, v(-63.28, 69.57) * mm, v(-63.43, 69.58) * mm, v(-63.5, 69.58) * mm]});
            skSolve(sketch);
        }
        {
            var Q0;
            Q0=qCreatedBy(makeId("Top.planeOp"),FACE);
            var sketch = newSketch(context, id + "F8", { "sketchPlane" : qUnion([Q0])});
            skCircle(sketch, "E6", {"center": v(55.4, 0) * mm, "radius": 5.08 * mm});
            skSolve(sketch);
        }
        {
            var Q0;
            Q0=makeQuery(id+"F8.imprint","IMPRINT",FACE,{"disambiguationData":[TD([[makeQuery(id+"F8.imprint","IMPRINT",EDGE,{"derivedFrom":sQuery(id+"F8.wireOp",EDGE,"E6")}),1.0]])]});
            var Q1;
            Q1=sQuery(id+"F7.wireOp",EDGE,"E5.0");
            sweep(context, id + "F9", {"profiles" : qUnion([Q0]), "path" : qUnion([Q1])});
        }
        {
            var Q0;
            Q0=makeQuery(id+"F4.opRevolve","SWEPT_BODY",BODY,{"disambiguationData":[OSD([sQuery(id+"F3.wireOp",EDGE,"E1"),sQuery(id+"F3.wireOp",EDGE,"E2"),sQuery(id+"F3.wireOp",EDGE,"E3")])]});
            deleteBodies(context, id + "F10", {"entities" : qUnion([Q0])});
        }
    });
